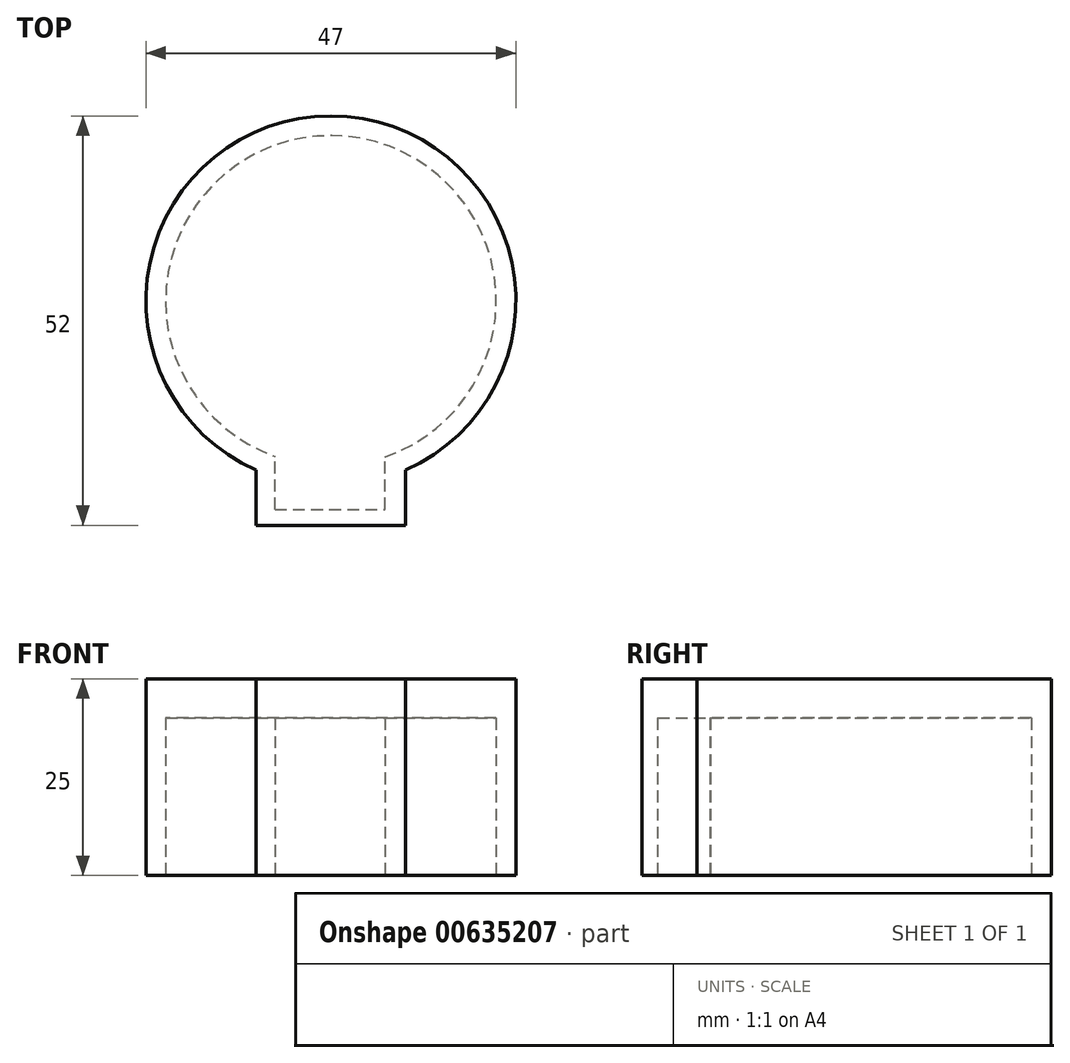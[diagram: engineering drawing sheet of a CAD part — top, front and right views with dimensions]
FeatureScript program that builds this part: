
annotation { "Feature Type Name" : "Feature", "Feature Type Description" : "" }
export const myFeature = defineFeature(function(context is Context, id is Id, definition is map)
    precondition{}
    {
        {
            var Q0;
            Q0=qCreatedBy(makeId("Top.planeOp"),FACE);
            var sketch = newSketch(context, id + "F0", { "sketchPlane" : qUnion([Q0])});
            skCircle(sketch, "E0", {"center": v(0, 0) * mm, "radius": 23.5 * mm});
            skSolve(sketch);
        }
        {
            var Q0;
            Q0 = qSketchRegion(id + "F0", true);
            var Q1;
            Q1 = qSketchRegion(id + "F2", true);
            extrude(context, id + "F1", {"entities" : qUnion([Q0, Q1]), "depth" : 25 * mm, "offsetDistance" : 25 * mm});
        }
        {
            var Q0;
            Q0=makeQuery(id+"F1.opExtrude","CAP_FACE",FACE,{"disambiguationData":[OSD([sQuery(id+"F0.wireOp",EDGE,"E0")])],"isStart":false});
            var sketch = newSketch(context, id + "F2", { "sketchPlane" : qUnion([Q0])});
            skPoint(sketch, "E1", {"position": v(0, -23.5) * mm});
            skLineSegment(sketch, "E2.bottom", {"start": v(9.5, -28.5) * mm, "end": v(-9.5, -28.5) * mm});
            skLineSegment(sketch, "E2.top", {"start": v(9.5, -18.5) * mm, "end": v(-9.5, -18.5) * mm});
            skLineSegment(sketch, "E2.left", {"start": v(9.5, -28.5) * mm, "end": v(9.5, -18.5) * mm});
            skLineSegment(sketch, "E2.right", {"start": v(-9.5, -28.5) * mm, "end": v(-9.5, -18.5) * mm});
            skSolve(sketch);
        }
        {
            var Q0;
            Q0 = qSketchRegion(id + "F2", true);
            extrude(context, id + "F3", {"entities" : qUnion([Q0]), "operationType" : NewBodyOperationType.ADD, "oppositeDirection" : true, "depth" : 25 * mm, "offsetDistance" : 25 * mm});
        }
        {
            var Q0;
            Q0=qCreatedBy(makeId("Top.planeOp"),FACE);
            var sketch = newSketch(context, id + "F4", { "sketchPlane" : qUnion([Q0])});
            skPoint(sketch, "E3", {"position": v(-0.12, -26.5) * mm});
            skLineSegment(sketch, "E4", {"start": v(0, 0) * mm, "end": v(-0.12, -26.5) * mm});
            skPoint(sketch, "E5", {"position": v(-7.12, -26.5) * mm});
            skPoint(sketch, "E6", {"position": v(6.88, -26.5) * mm});
            skPoint(sketch, "E7", {"position": v(6.88, 0) * mm});
            skPoint(sketch, "E8", {"position": v(-7.12, 0) * mm});
            skLineSegment(sketch, "E9", {"start": v(-7.12, -26.5) * mm, "end": v(6.88, -26.5) * mm});
            skCircle(sketch, "E10", {"center": v(0, 0) * mm, "radius": 21 * mm});
            skLineSegment(sketch, "E11", {"start": v(-7.12, -26.5) * mm, "end": v(-7.12, -19.76) * mm});
            skLineSegment(sketch, "E12", {"start": v(6.88, -26.5) * mm, "end": v(6.88, -19.84) * mm});
            skSolve(sketch);
        }
        {
            var Q0;
            {var subQ5=sQuery(id+"F4.wireOp",EDGE,"E11");Q0=makeQuery(id+"F4.imprint","IMPRINT",FACE,{"disambiguationData":[TD([[makeQuery(id+"F4.imprint","IMPRINT",EDGE,{"derivedFrom":subQ5}),-1.0]])]});}
            var Q1;
            {var subQ5=sQuery(id+"F4.wireOp",EDGE,"E12");Q1=makeQuery(id+"F4.imprint","IMPRINT",FACE,{"disambiguationData":[TD([[makeQuery(id+"F4.imprint","IMPRINT",EDGE,{"derivedFrom":subQ5}),1.0]])]});}
            var Q2;
            {var subQ0=sQuery(id+"F4.wireOp",EDGE,"E10");var subQ1=makeQuery(id+"F4.imprint","INTERSECT",VERTEX,{"derivedFrom":[subQ0,sQuery(id+"F4.wireOp",EDGE,"E11")]});Q2=makeQuery(id+"F4.imprint","IMPRINT",FACE,{"disambiguationData":[TD([[makeQuery(id+"F4.imprint","IMPRINT",EDGE,{"disambiguationData":[TD([[subQ1,-1.0]])],"derivedFrom":subQ0}),1.0]])]});}
            extrude(context, id + "F5", {"entities" : qUnion([Q0, Q1, Q2]), "operationType" : NewBodyOperationType.REMOVE, "depth" : 20 * mm, "offsetDistance" : 25 * mm});
        }
    });
